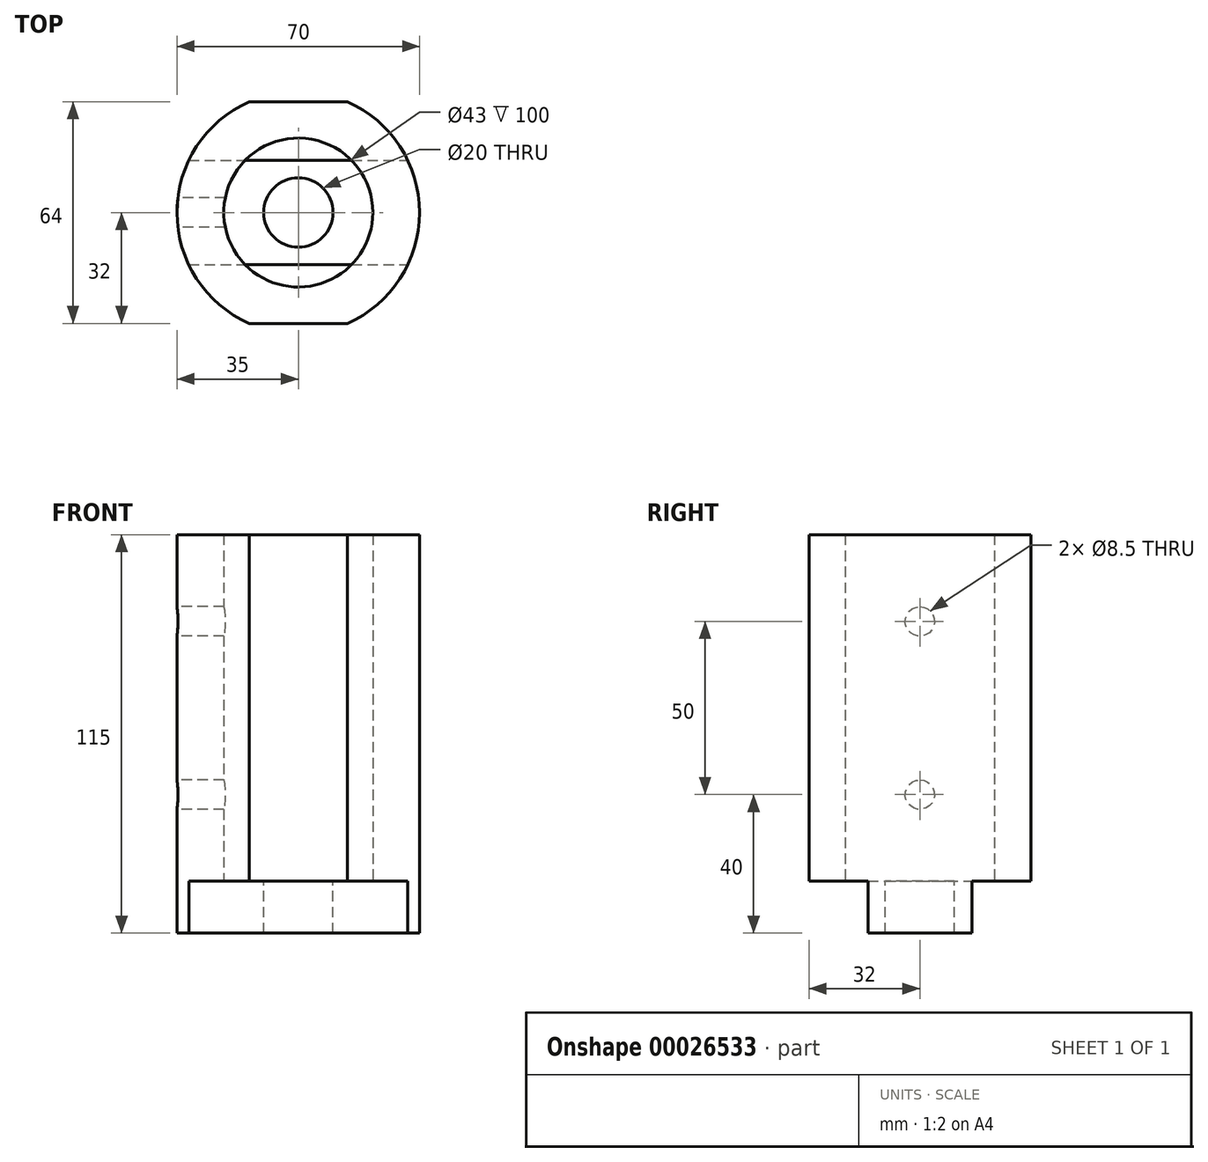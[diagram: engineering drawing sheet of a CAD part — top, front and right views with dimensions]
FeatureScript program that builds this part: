
annotation { "Feature Type Name" : "Feature", "Feature Type Description" : "" }
export const myFeature = defineFeature(function(context is Context, id is Id, definition is map)
    precondition{}
    {
        {
            var Q0;
            Q0=qCreatedBy(makeId("Top.planeOp"),FACE);
            var sketch = newSketch(context, id + "F0", { "sketchPlane" : qUnion([Q0])});
            skArc(sketch, "E0", {"start": v(-14.18, 32) * mm, "mid": v(-35, 0) * mm, "end": v(-14.18, -32) * mm});
            skCircle(sketch, "E1", {"center": v(0, 0) * mm, "radius": 21.5 * mm});
            skLineSegment(sketch, "E2.0", {"start": v(-14.18, 32) * mm, "end": v(14.18, 32) * mm});
            skLineSegment(sketch, "E3.0", {"start": v(-14.18, -32) * mm, "end": v(14.18, -32) * mm});
            skArc(sketch, "E4.trimOffspring", {"start": v(14.18, -32) * mm, "mid": v(35, 0) * mm, "end": v(14.18, 32) * mm});
            skSolve(sketch);
        }
        {
            var Q0;
            Q0=makeQuery(id+"F0.imprint","IMPRINT",FACE,{"disambiguationData":[TD([[makeQuery(id+"F0.imprint","IMPRINT",EDGE,{"derivedFrom":sQuery(id+"F0.wireOp",EDGE,"E0")}),1.0]])]});
            extrude(context, id + "F1", {"entities" : qUnion([Q0]), "depth" : 100 * mm});
        }
        {
            var Q0;
            Q0=makeQuery(id+"F1.opExtrude","CAP_FACE",FACE,{"disambiguationData":[OSD([sQuery(id+"F0.wireOp",EDGE,"E0"),sQuery(id+"F0.wireOp",EDGE,"E1"),sQuery(id+"F0.wireOp",EDGE,"E2.0"),sQuery(id+"F0.wireOp",EDGE,"E3.0"),sQuery(id+"F0.wireOp",EDGE,"E4.trimOffspring")])],"isStart":true});
            var sketch = newSketch(context, id + "F2", { "sketchPlane" : qUnion([Q0])});
            skCircle(sketch, "E5.0", {"center": v(0, 0) * mm, "radius": 21.5 * mm, "construction": true});
            skArc(sketch, "E6.0", {"start": v(-14.18, -32) * mm, "mid": v(-35, 0) * mm, "end": v(-14.18, 32) * mm});
            skLineSegment(sketch, "E7.0", {"start": v(-14.18, 32) * mm, "end": v(14.18, 32) * mm});
            skLineSegment(sketch, "E8.0", {"start": v(-14.18, -32) * mm, "end": v(14.18, -32) * mm});
            skArc(sketch, "E9.0", {"start": v(14.18, 32) * mm, "mid": v(35, 0) * mm, "end": v(14.18, -32) * mm});
            skLineSegment(sketch, "E10", {"start": v(0, 0) * mm, "end": v(-35, 0) * mm, "construction": true});
            skLineSegment(sketch, "E11", {"start": v(-35, 0) * mm, "end": v(35, 0) * mm, "construction": true});
            skLineSegment(sketch, "E12.0", {"start": v(-31.61, -15.02) * mm, "end": v(31.61, -15.02) * mm});
            skLineSegment(sketch, "E13.0", {"start": v(-31.61, 15.02) * mm, "end": v(31.61, 15.02) * mm});
            skCircle(sketch, "E14", {"center": v(0, 0) * mm, "radius": 10 * mm});
            skSolve(sketch);
        }
        {
            var Q0;
            {var subQ3=sQuery(id+"F2.wireOp",EDGE,"E12.0");var subQ5=sQuery(id+"F2.wireOp",EDGE,"E6.0");var subQ7=makeQuery(id+"F2.imprint","INTERSECT",VERTEX,{"derivedFrom":[subQ5,subQ3]});Q0=makeQuery(id+"F2.imprint","IMPRINT",FACE,{"disambiguationData":[TD([[makeQuery(id+"F2.imprint","IMPRINT",EDGE,{"disambiguationData":[TD([[subQ7,-1.0]])],"derivedFrom":subQ5}),-1.0]])]});}
            var Q1;
            {var subQ0=makeQuery(id+"F1.opExtrude","CAP_EDGE",EDGE,{"disambiguationData":[OSD([sQuery(id+"F0.wireOp",EDGE,"E1")])],"isStart":true});var subQ3=sQuery(id+"F2.wireOp",EDGE,"E12.0");var subQ6=makeQuery(id+"F2.imprint","INTERSECT",VERTEX,{"disambiguationData":[OD(0.0)],"derivedFrom":[subQ0,subQ3]});Q1=makeQuery(id+"F2.imprint","IMPRINT",FACE,{"disambiguationData":[TD([[makeQuery(id+"F2.imprint","IMPRINT",EDGE,{"disambiguationData":[TD([[subQ6,-1.0]])],"derivedFrom":subQ3}),1.0]])]});}
            var Q2;
            {var subQ3=sQuery(id+"F2.wireOp",EDGE,"E12.0");var subQ5=sQuery(id+"F2.wireOp",EDGE,"E9.0");var subQ7=makeQuery(id+"F2.imprint","INTERSECT",VERTEX,{"derivedFrom":[subQ5,subQ3]});Q2=makeQuery(id+"F2.imprint","IMPRINT",FACE,{"disambiguationData":[TD([[makeQuery(id+"F2.imprint","IMPRINT",EDGE,{"disambiguationData":[TD([[subQ7,1.0]])],"derivedFrom":subQ5}),-1.0]])]});}
            extrude(context, id + "F3", {"entities" : qUnion([Q0, Q1, Q2]), "operationType" : NewBodyOperationType.ADD, "depth" : 15 * mm});
        }
        {
            var Q0;
            Q0=qCreatedBy(makeId("Right.planeOp"),FACE);
            cPlane(context, id + "F4", {"entities" : qUnion([Q0]), "cplaneType" : CPlaneType.OFFSET, "offset" : 35 * mm, "oppositeDirection" : true, "width" : 150 * mm, "height" : 150 * mm});
        }
        {
            var Q0;
            Q0=qCreatedBy(id+"F4.planeOp",FACE);
            var sketch = newSketch(context, id + "F5", { "sketchPlane" : qUnion([Q0])});
            skLineSegment(sketch, "E15.0", {"start": v(32, 100) * mm, "end": v(32, 0) * mm});
            skLineSegment(sketch, "E16.0", {"start": v(-32, 100) * mm, "end": v(-32, 0) * mm});
            skCircle(sketch, "E17", {"center": v(0, 75) * mm, "radius": 4.25 * mm});
            skCircle(sketch, "E18", {"center": v(0, 25) * mm, "radius": 4.25 * mm});
            skSolve(sketch);
        }
        {
            var Q0;
            Q0=makeQuery(id+"F5.imprint","IMPRINT",FACE,{"disambiguationData":[TD([[makeQuery(id+"F5.imprint","IMPRINT",EDGE,{"derivedFrom":sQuery(id+"F5.wireOp",EDGE,"E17")}),1.0]])]});
            var Q1;
            Q1=makeQuery(id+"F5.imprint","IMPRINT",FACE,{"disambiguationData":[TD([[makeQuery(id+"F5.imprint","IMPRINT",EDGE,{"derivedFrom":sQuery(id+"F5.wireOp",EDGE,"E18")}),1.0]])]});
            extrude(context, id + "F6", {"entities" : qUnion([Q0, Q1]), "operationType" : NewBodyOperationType.REMOVE, "depth" : 35 * mm});
        }
    });
